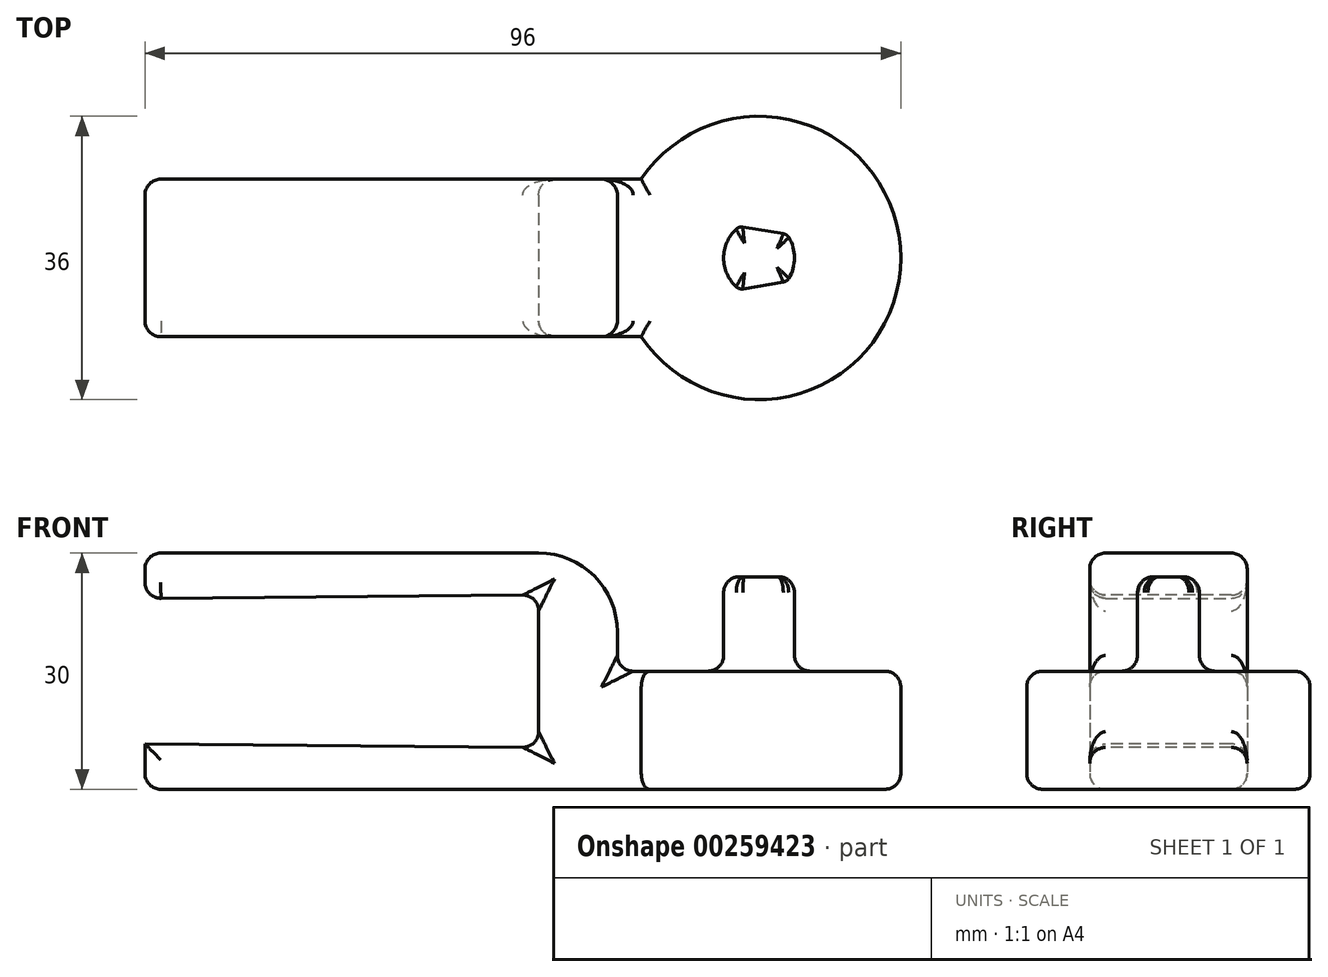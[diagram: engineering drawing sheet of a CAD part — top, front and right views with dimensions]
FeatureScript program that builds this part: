
annotation { "Feature Type Name" : "Feature", "Feature Type Description" : "" }
export const myFeature = defineFeature(function(context is Context, id is Id, definition is map)
    precondition{}
    {
        {
            var Q0;
            Q0=qCreatedBy(makeId("Top.planeOp"),FACE);
            var sketch = newSketch(context, id + "F0", { "sketchPlane" : qUnion([Q0])});
            skCircle(sketch, "E0", {"center": v(18, 10) * mm, "radius": 18 * mm});
            skLineSegment(sketch, "E1.bottom", {"start": v(3.03, 0) * mm, "end": v(-60, 0) * mm});
            skLineSegment(sketch, "E1.top", {"start": v(3.03, 20) * mm, "end": v(-60, 20) * mm});
            skLineSegment(sketch, "E1.left", {"start": v(0, 0) * mm, "end": v(0, 20) * mm});
            skLineSegment(sketch, "E1.right", {"start": v(-60, 0) * mm, "end": v(-60, 20) * mm});
            skSolve(sketch);
        }
        {
            var Q0;
            {var subQ6=sQuery(id+"F0.wireOp",EDGE,"E1.right");Q0=makeQuery(id+"F0.imprint","IMPRINT",FACE,{"disambiguationData":[TD([[makeQuery(id+"F0.imprint","IMPRINT",EDGE,{"derivedFrom":subQ6}),-1.0]])]});}
            extrude(context, id + "F1", {"entities" : qUnion([Q0]), "depth" : 30 * mm});
        }
        {
            var Q0;
            Q0=qSketchRegion(id+"F0",true);
            extrude(context, id + "F2", {"entities" : qUnion([Q0]), "operationType" : NewBodyOperationType.ADD, "depth" : 15 * mm});
        }
        {
            var Q0;
            Q0=makeQuery(id+"F1.opExtrude","SWEPT_FACE",FACE,{"disambiguationData":[OSD([sQuery(id+"F0.wireOp",EDGE,"E1.right")])]});
            var sketch = newSketch(context, id + "F3", { "sketchPlane" : qUnion([Q0])});
            skLineSegment(sketch, "E2.bottom", {"start": v(-20, 5.75) * mm, "end": v(0, 5.75) * mm});
            skLineSegment(sketch, "E2.top", {"start": v(-20, 24.25) * mm, "end": v(0, 24.25) * mm});
            skLineSegment(sketch, "E2.left", {"start": v(-20, 5.75) * mm, "end": v(-20, 24.25) * mm});
            skLineSegment(sketch, "E2.right", {"start": v(0, 5.75) * mm, "end": v(0, 24.25) * mm});
            skSolve(sketch);
        }
        {
            var Q0;
            Q0=qSketchRegion(id+"F3",true);
            extrude(context, id + "F4", {"entities" : qUnion([Q0]), "operationType" : NewBodyOperationType.REMOVE, "oppositeDirection" : true, "depth" : 50 * mm, "hasDraft" : true, "draftAngle" : 0.5 * degree});
        }
        {
            var Q0;
            Q0=makeQuery(id+"F2.opExtrude","CAP_FACE",FACE,{"disambiguationData":[OSD([sQuery(id+"F0.wireOp",EDGE,"E0"),sQuery(id+"F0.wireOp",EDGE,"E1.bottom"),sQuery(id+"F0.wireOp",EDGE,"E1.top"),sQuery(id+"F0.wireOp",EDGE,"E1.right")])],"isStart":false});
            var sketch = newSketch(context, id + "F5", { "sketchPlane" : qUnion([Q0])});
            skLineSegment(sketch, "E3", {"start": v(0, 10) * mm, "end": v(35.98, 10) * mm, "construction": true});
            skArc(sketch, "E4", {"start": v(15.1, 13.67) * mm, "mid": v(13.5, 10) * mm, "end": v(15.1, 6.33) * mm});
            skArc(sketch, "E5", {"start": v(21.77, 7.4) * mm, "mid": v(22.5, 10) * mm, "end": v(21.77, 12.6) * mm});
            skLineSegment(sketch, "E6", {"start": v(15.95, 13.92) * mm, "end": v(21.08, 13.07) * mm});
            skLineSegment(sketch, "E7", {"start": v(15.95, 6.08) * mm, "end": v(21.08, 6.93) * mm});
            skPoint(sketch, "E8.visualSharp", {"position": v(15.5, 14) * mm});
            skArc(sketch, "E8.filletArc", {"start": v(15.95, 13.92) * mm, "mid": v(15.5, 13.9) * mm, "end": v(15.1, 13.67) * mm});
            skPoint(sketch, "E9.visualSharp", {"position": v(21.5, 13) * mm});
            skArc(sketch, "E9.filletArc", {"start": v(21.77, 12.6) * mm, "mid": v(21.47, 12.91) * mm, "end": v(21.08, 13.07) * mm});
            skPoint(sketch, "E10.visualSharp", {"position": v(21.5, 7) * mm});
            skArc(sketch, "E10.filletArc", {"start": v(21.08, 6.93) * mm, "mid": v(21.47, 7.09) * mm, "end": v(21.77, 7.4) * mm});
            skPoint(sketch, "E11.visualSharp", {"position": v(15.5, 6) * mm});
            skArc(sketch, "E11.filletArc", {"start": v(15.1, 6.33) * mm, "mid": v(15.5, 6.1) * mm, "end": v(15.95, 6.08) * mm});
            skSolve(sketch);
        }
        {
            var Q0;
            Q0=makeQuery(id+"F5.imprint","IMPRINT",FACE,{"disambiguationData":[TD([[makeQuery(id+"F5.imprint","IMPRINT",EDGE,{"derivedFrom":sQuery(id+"F5.wireOp",EDGE,"E4")}),1.0]])]});
            extrude(context, id + "F6", {"entities" : qUnion([Q0]), "operationType" : NewBodyOperationType.ADD, "depth" : 12 * mm});
        }
        {
            var Q0;
            Q0=makeQuery(id+"F6.opExtrude","CAP_FACE",FACE,{"disambiguationData":[OSD([sQuery(id+"F5.wireOp",EDGE,"E4"),sQuery(id+"F5.wireOp",EDGE,"E5"),sQuery(id+"F5.wireOp",EDGE,"E6"),sQuery(id+"F5.wireOp",EDGE,"E7"),sQuery(id+"F5.wireOp",EDGE,"E8.filletArc"),sQuery(id+"F5.wireOp",EDGE,"E9.filletArc"),sQuery(id+"F5.wireOp",EDGE,"E10.filletArc"),sQuery(id+"F5.wireOp",EDGE,"E11.filletArc")])],"isStart":false});
            var Q1;
            Q1=makeQuery(id+"F2.opExtrude","CAP_EDGE",EDGE,{"disambiguationData":[OSD([sQuery(id+"F0.wireOp",EDGE,"E0")])],"isStart":false});
            var Q2;
            Q2=makeQuery(id+"F2.opExtrude","CAP_EDGE",EDGE,{"disambiguationData":[OSD([sQuery(id+"F0.wireOp",EDGE,"E0")])],"isStart":true});
            var Q3;
            Q3=makeQuery(id+"F2.opExtrude","CAP_EDGE",EDGE,{"disambiguationData":[OSD([sQuery(id+"F0.wireOp",EDGE,"E1.bottom")])],"isStart":false});
            var Q4;
            Q4=makeQuery(id+"F2.opExtrude","CAP_EDGE",EDGE,{"disambiguationData":[OSD([sQuery(id+"F0.wireOp",EDGE,"E1.top")])],"isStart":false});
            var Q5;
            Q5=makeQuery(id+"F1.opExtrude","SWEPT_EDGE",EDGE,{"disambiguationData":[OSD([sQuery(id+"F0.wireOp",EDGE,"E1.bottom"),sQuery(id+"F0.wireOp",EDGE,"E1.left")])]});
            var Q6;
            Q6=makeQuery(id+"F1.opExtrude","SWEPT_EDGE",EDGE,{"disambiguationData":[OSD([sQuery(id+"F0.wireOp",EDGE,"E1.top"),sQuery(id+"F0.wireOp",EDGE,"E1.left")])]});
            var Q7;
            Q7=makeQuery(id+"F4.boolean.opBoolean","COPY",EDGE,{"derivedFrom":makeQuery(id+"F4.opExtrude","CAP_EDGE",EDGE,{"disambiguationData":[OSD([sQuery(id+"F3.wireOp",EDGE,"E2.right")])],"isStart":false})});
            var Q8;
            Q8=makeQuery(id+"F4.boolean.opBoolean","COPY",EDGE,{"derivedFrom":makeQuery(id+"F4.opExtrude","CAP_EDGE",EDGE,{"disambiguationData":[OSD([sQuery(id+"F3.wireOp",EDGE,"E2.left")])],"isStart":false})});
            var Q9;
            Q9=makeQuery(id+"F4.boolean.opBoolean","COPY",EDGE,{"derivedFrom":makeQuery(id+"F4.opExtrude","SWEPT_EDGE",EDGE,{"disambiguationData":[OSD([sQuery(id+"F0.wireOp",EDGE,"E1.top"),sQuery(id+"F0.wireOp",EDGE,"E1.right"),sQuery(id+"F3.wireOp",EDGE,"E2.top"),sQuery(id+"F3.wireOp",EDGE,"E2.left")])]})});
            var Q10;
            Q10=makeQuery(id+"F1.opExtrude","CAP_EDGE",EDGE,{"disambiguationData":[OSD([sQuery(id+"F0.wireOp",EDGE,"E1.top")])],"isStart":false});
            var Q11;
            Q11=makeQuery(id+"F4.boolean.opBoolean","COPY",EDGE,{"derivedFrom":makeQuery(id+"F4.opExtrude","SWEPT_EDGE",EDGE,{"disambiguationData":[OSD([sQuery(id+"F0.wireOp",EDGE,"E1.top"),sQuery(id+"F0.wireOp",EDGE,"E1.right"),sQuery(id+"F3.wireOp",EDGE,"E2.bottom"),sQuery(id+"F3.wireOp",EDGE,"E2.left")])]})});
            var Q12;
            {var subQ0=sQuery(id+"F0.wireOp",EDGE,"E1.top");Q12=makeQuery(id+"F2.boolean.opBoolean","MERGE",EDGE,{"derivedFrom":[makeQuery(id+"F1.opExtrude","CAP_EDGE",EDGE,{"disambiguationData":[OSD([subQ0])],"isStart":true}),makeQuery(id+"F2.opExtrude","CAP_EDGE",EDGE,{"disambiguationData":[OSD([subQ0])],"isStart":true})]});}
            var Q13;
            Q13=makeQuery(id+"F1.opExtrude","CAP_EDGE",EDGE,{"disambiguationData":[OSD([sQuery(id+"F0.wireOp",EDGE,"E1.bottom")])],"isStart":false});
            var Q14;
            Q14=makeQuery(id+"F4.boolean.opBoolean","COPY",EDGE,{"derivedFrom":makeQuery(id+"F4.opExtrude","SWEPT_EDGE",EDGE,{"disambiguationData":[OSD([sQuery(id+"F0.wireOp",EDGE,"E1.bottom"),sQuery(id+"F0.wireOp",EDGE,"E1.right"),sQuery(id+"F3.wireOp",EDGE,"E2.top"),sQuery(id+"F3.wireOp",EDGE,"E2.right")])]})});
            var Q15;
            Q15=makeQuery(id+"F4.boolean.opBoolean","COPY",EDGE,{"derivedFrom":makeQuery(id+"F4.opExtrude","SWEPT_EDGE",EDGE,{"disambiguationData":[OSD([sQuery(id+"F0.wireOp",EDGE,"E1.bottom"),sQuery(id+"F0.wireOp",EDGE,"E1.right"),sQuery(id+"F3.wireOp",EDGE,"E2.bottom"),sQuery(id+"F3.wireOp",EDGE,"E2.right")])]})});
            var Q16;
            {var subQ0=sQuery(id+"F0.wireOp",EDGE,"E1.bottom");Q16=makeQuery(id+"F2.boolean.opBoolean","MERGE",EDGE,{"derivedFrom":[makeQuery(id+"F1.opExtrude","CAP_EDGE",EDGE,{"disambiguationData":[OSD([subQ0])],"isStart":true}),makeQuery(id+"F2.opExtrude","CAP_EDGE",EDGE,{"disambiguationData":[OSD([subQ0])],"isStart":true})]});}
            var Q17;
            Q17=makeQuery(id+"F1.opExtrude","CAP_EDGE",EDGE,{"disambiguationData":[OSD([sQuery(id+"F0.wireOp",EDGE,"E1.right")])],"isStart":false});
            var Q18;
            Q18=makeQuery(id+"F4.boolean.opBoolean","COPY",EDGE,{"derivedFrom":makeQuery(id+"F4.opExtrude","CAP_EDGE",EDGE,{"disambiguationData":[OSD([sQuery(id+"F3.wireOp",EDGE,"E2.top")])],"isStart":true})});
            var Q19;
            Q19=makeQuery(id+"F4.boolean.opBoolean","COPY",EDGE,{"derivedFrom":makeQuery(id+"F4.opExtrude","CAP_EDGE",EDGE,{"disambiguationData":[OSD([sQuery(id+"F3.wireOp",EDGE,"E2.bottom")])],"isStart":true})});
            var Q20;
            Q20=makeQuery(id+"F1.opExtrude","CAP_EDGE",EDGE,{"disambiguationData":[OSD([sQuery(id+"F0.wireOp",EDGE,"E1.right")])],"isStart":true});
            var Q21;
            {var subQ0=sQuery(id+"F0.wireOp",EDGE,"E1.bottom");var subQ1=sQuery(id+"F0.wireOp",EDGE,"E1.right");Q21=makeQuery(id+"F4.boolean.opBoolean","SPLIT",EDGE,{"disambiguationData":[TD([makeQuery(id+"F4.opExtrude","SWEPT_FACE",FACE,{"disambiguationData":[OSD([sQuery(id+"F3.wireOp",EDGE,"E2.top")])]})])],"derivedFrom":makeQuery(id+"F1.opExtrude","SWEPT_EDGE",EDGE,{"disambiguationData":[OSD([subQ0,subQ1])]})});}
            var Q22;
            {var subQ0=sQuery(id+"F0.wireOp",EDGE,"E1.top");var subQ1=sQuery(id+"F0.wireOp",EDGE,"E1.right");Q22=makeQuery(id+"F4.boolean.opBoolean","SPLIT",EDGE,{"disambiguationData":[TD([makeQuery(id+"F4.opExtrude","SWEPT_FACE",FACE,{"disambiguationData":[OSD([sQuery(id+"F3.wireOp",EDGE,"E2.top")])]})])],"derivedFrom":makeQuery(id+"F1.opExtrude","SWEPT_EDGE",EDGE,{"disambiguationData":[OSD([subQ0,subQ1])]})});}
            var Q23;
            {var subQ0=sQuery(id+"F0.wireOp",EDGE,"E1.right");var subQ1=sQuery(id+"F0.wireOp",EDGE,"E1.top");Q23=makeQuery(id+"F4.boolean.opBoolean","SPLIT",EDGE,{"disambiguationData":[TD([makeQuery(id+"F4.opExtrude","SWEPT_FACE",FACE,{"disambiguationData":[OSD([sQuery(id+"F3.wireOp",EDGE,"E2.bottom")])]})])],"derivedFrom":makeQuery(id+"F1.opExtrude","SWEPT_EDGE",EDGE,{"disambiguationData":[OSD([subQ1,subQ0])]})});}
            var Q24;
            {var subQ0=sQuery(id+"F0.wireOp",EDGE,"E1.right");var subQ2=sQuery(id+"F0.wireOp",EDGE,"E1.bottom");Q24=makeQuery(id+"F4.boolean.opBoolean","SPLIT",EDGE,{"disambiguationData":[TD([makeQuery(id+"F4.opExtrude","SWEPT_FACE",FACE,{"disambiguationData":[OSD([sQuery(id+"F3.wireOp",EDGE,"E2.bottom")])]})])],"derivedFrom":makeQuery(id+"F1.opExtrude","SWEPT_EDGE",EDGE,{"disambiguationData":[OSD([subQ2,subQ0])]})});}
            var Q25;
            {var subQ0=sQuery(id+"F0.wireOp",EDGE,"E1.bottom");Q25=makeQuery(id+"F4.boolean.opBoolean","INTERSECT",EDGE,{"derivedFrom":[makeQuery(id+"F2.boolean.opBoolean","MERGE",FACE,{"derivedFrom":[makeQuery(id+"F1.opExtrude","SWEPT_FACE",FACE,{"disambiguationData":[OSD([subQ0])]}),makeQuery(id+"F2.opExtrude","SWEPT_FACE",FACE,{"disambiguationData":[OSD([subQ0])]})]}),makeQuery(id+"F4.opExtrude","SWEPT_FACE",FACE,{"disambiguationData":[OSD([sQuery(id+"F3.wireOp",EDGE,"E2.bottom")])]})]});}
            var Q26;
            {var subQ0=sQuery(id+"F0.wireOp",EDGE,"E1.bottom");Q26=makeQuery(id+"F4.boolean.opBoolean","INTERSECT",EDGE,{"derivedFrom":[makeQuery(id+"F2.boolean.opBoolean","MERGE",FACE,{"derivedFrom":[makeQuery(id+"F1.opExtrude","SWEPT_FACE",FACE,{"disambiguationData":[OSD([subQ0])]}),makeQuery(id+"F2.opExtrude","SWEPT_FACE",FACE,{"disambiguationData":[OSD([subQ0])]})]}),makeQuery(id+"F4.opExtrude","CAP_FACE",FACE,{"disambiguationData":[OSD([sQuery(id+"F3.wireOp",EDGE,"E2.bottom"),sQuery(id+"F3.wireOp",EDGE,"E2.top"),sQuery(id+"F3.wireOp",EDGE,"E2.left"),sQuery(id+"F3.wireOp",EDGE,"E2.right")])],"isStart":false})]});}
            var Q27;
            {var subQ0=sQuery(id+"F0.wireOp",EDGE,"E1.bottom");Q27=makeQuery(id+"F4.boolean.opBoolean","INTERSECT",EDGE,{"derivedFrom":[makeQuery(id+"F2.boolean.opBoolean","MERGE",FACE,{"derivedFrom":[makeQuery(id+"F1.opExtrude","SWEPT_FACE",FACE,{"disambiguationData":[OSD([subQ0])]}),makeQuery(id+"F2.opExtrude","SWEPT_FACE",FACE,{"disambiguationData":[OSD([subQ0])]})]}),makeQuery(id+"F4.opExtrude","SWEPT_FACE",FACE,{"disambiguationData":[OSD([sQuery(id+"F3.wireOp",EDGE,"E2.top")])]})]});}
            var Q28;
            {var subQ0=sQuery(id+"F0.wireOp",EDGE,"E1.top");Q28=makeQuery(id+"F4.boolean.opBoolean","INTERSECT",EDGE,{"derivedFrom":[makeQuery(id+"F2.boolean.opBoolean","MERGE",FACE,{"derivedFrom":[makeQuery(id+"F1.opExtrude","SWEPT_FACE",FACE,{"disambiguationData":[OSD([subQ0])]}),makeQuery(id+"F2.opExtrude","SWEPT_FACE",FACE,{"disambiguationData":[OSD([subQ0])]})]}),makeQuery(id+"F4.opExtrude","SWEPT_FACE",FACE,{"disambiguationData":[OSD([sQuery(id+"F3.wireOp",EDGE,"E2.top")])]})]});}
            var Q29;
            {var subQ0=sQuery(id+"F0.wireOp",EDGE,"E1.top");Q29=makeQuery(id+"F4.boolean.opBoolean","INTERSECT",EDGE,{"derivedFrom":[makeQuery(id+"F2.boolean.opBoolean","MERGE",FACE,{"derivedFrom":[makeQuery(id+"F1.opExtrude","SWEPT_FACE",FACE,{"disambiguationData":[OSD([subQ0])]}),makeQuery(id+"F2.opExtrude","SWEPT_FACE",FACE,{"disambiguationData":[OSD([subQ0])]})]}),makeQuery(id+"F4.opExtrude","CAP_FACE",FACE,{"disambiguationData":[OSD([sQuery(id+"F3.wireOp",EDGE,"E2.bottom"),sQuery(id+"F3.wireOp",EDGE,"E2.top"),sQuery(id+"F3.wireOp",EDGE,"E2.left"),sQuery(id+"F3.wireOp",EDGE,"E2.right")])],"isStart":false})]});}
            var Q30;
            {var subQ0=sQuery(id+"F0.wireOp",EDGE,"E1.top");Q30=makeQuery(id+"F4.boolean.opBoolean","INTERSECT",EDGE,{"derivedFrom":[makeQuery(id+"F2.boolean.opBoolean","MERGE",FACE,{"derivedFrom":[makeQuery(id+"F1.opExtrude","SWEPT_FACE",FACE,{"disambiguationData":[OSD([subQ0])]}),makeQuery(id+"F2.opExtrude","SWEPT_FACE",FACE,{"disambiguationData":[OSD([subQ0])]})]}),makeQuery(id+"F4.opExtrude","SWEPT_FACE",FACE,{"disambiguationData":[OSD([sQuery(id+"F3.wireOp",EDGE,"E2.bottom")])]})]});}
            fillet(context, id + "F7", {"entities" : qUnion([Q0, Q1, Q2, Q3, Q4, Q5, Q6, Q7, Q8, Q9, Q10, Q11, Q12, Q13, Q14, Q15, Q16, Q17, Q18, Q19, Q20, Q21, Q22, Q23, Q24, Q25, Q26, Q27, Q28, Q29, Q30]), "radius" : 2 * mm, "tangentPropagation" : true, "allowEdgeOverflow" : false});
        }
        {
            var Q0;
            Q0=makeQuery(id+"F1.opExtrude","CAP_EDGE",EDGE,{"disambiguationData":[OSD([sQuery(id+"F0.wireOp",EDGE,"E1.left")])],"isStart":false});
            fillet(context, id + "F8", {"entities" : qUnion([Q0]), "radius" : 10 * mm, "tangentPropagation" : true, "allowEdgeOverflow" : false});
        }
        {
            var Q0;
            Q0=makeQuery(id+"F2.opExtrude","CAP_FACE",FACE,{"disambiguationData":[OSD([sQuery(id+"F0.wireOp",EDGE,"E0"),sQuery(id+"F0.wireOp",EDGE,"E1.bottom"),sQuery(id+"F0.wireOp",EDGE,"E1.top"),sQuery(id+"F0.wireOp",EDGE,"E1.right")])],"isStart":false});
            var Q1;
            Q1=makeQuery(id+"F4.boolean.opBoolean","COPY",EDGE,{"derivedFrom":makeQuery(id+"F4.opExtrude","CAP_EDGE",EDGE,{"disambiguationData":[OSD([sQuery(id+"F3.wireOp",EDGE,"E2.top")])],"isStart":false})});
            var Q2;
            Q2=makeQuery(id+"F4.boolean.opBoolean","COPY",EDGE,{"derivedFrom":makeQuery(id+"F4.opExtrude","CAP_EDGE",EDGE,{"disambiguationData":[OSD([sQuery(id+"F3.wireOp",EDGE,"E2.bottom")])],"isStart":false})});
            fillet(context, id + "F9", {"entities" : qUnion([Q0, Q1, Q2]), "radius" : 2 * mm, "tangentPropagation" : true, "allowEdgeOverflow" : false});
        }
    });
